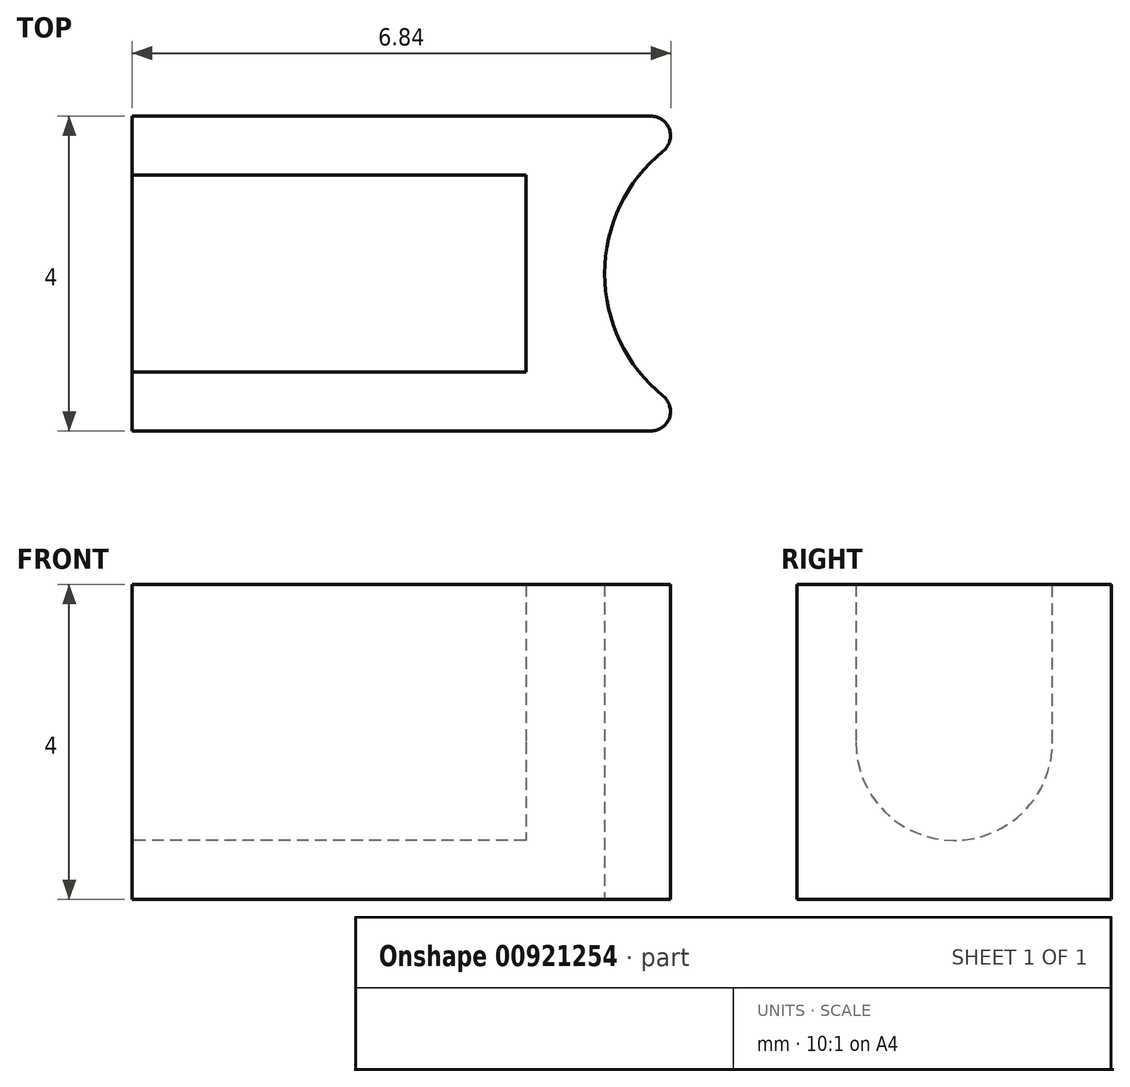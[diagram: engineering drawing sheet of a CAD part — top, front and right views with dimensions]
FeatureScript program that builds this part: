
annotation { "Feature Type Name" : "Feature", "Feature Type Description" : "" }
export const myFeature = defineFeature(function(context is Context, id is Id, definition is map)
    precondition{}
    {
        {
            var Q0;
            Q0=qCreatedBy(makeId("Top.planeOp"),FACE);
            var sketch = newSketch(context, id + "F0", { "sketchPlane" : qUnion([Q0])});
            skCircle(sketch, "E0", {"center": v(0, 0) * mm, "radius": 2 * mm});
            skLineSegment(sketch, "E1.bottom", {"start": v(0, 2) * mm, "end": v(-8, 2) * mm});
            skLineSegment(sketch, "E1.top", {"start": v(0, -2) * mm, "end": v(-8, -2) * mm});
            skLineSegment(sketch, "E1.left", {"start": v(0, 2) * mm, "end": v(0, -2) * mm});
            skLineSegment(sketch, "E1.right", {"start": v(-8, 2) * mm, "end": v(-8, -2) * mm});
            skSolve(sketch);
        }
        {
            var Q0;
            {var subQ1=sQuery(id+"F0.wireOp",EDGE,"E1.bottom");Q0=makeQuery(id+"F0.imprint","IMPRINT",FACE,{"disambiguationData":[TD([[makeQuery(id+"F0.imprint","IMPRINT",EDGE,{"derivedFrom":subQ1}),1.0]])]});}
            extrude(context, id + "F1", {"entities" : qUnion([Q0]), "depth" : 4 * mm, "offsetDistance" : 25 * mm});
        }
        {
            var Q0;
            Q0=makeQuery(id+"F1.opExtrude","SWEPT_FACE",FACE,{"disambiguationData":[OSD([sQuery(id+"F0.wireOp",EDGE,"E1.right")])]});
            var sketch = newSketch(context, id + "F2", { "sketchPlane" : qUnion([Q0])});
            skCircle(sketch, "E2", {"center": v(0, 2) * mm, "radius": 1.25 * mm});
            skPoint(sketch, "E2.centerSnap0", {"position": v(-2, 2) * mm});
            skLineSegment(sketch, "E3", {"start": v(-1.25, 2) * mm, "end": v(-1.25, 4) * mm});
            skLineSegment(sketch, "E4", {"start": v(-1.25, 4) * mm, "end": v(1.25, 4) * mm});
            skLineSegment(sketch, "E5", {"start": v(1.25, 4) * mm, "end": v(1.25, 2) * mm});
            skSolve(sketch);
        }
        {
            var Q0;
            Q0=makeQuery(id+"F2.imprint","IMPRINT",FACE,{"disambiguationData":[TD([[makeQuery(id+"F2.imprint","IMPRINT",EDGE,{"derivedFrom":sQuery(id+"F2.wireOp",EDGE,"E2")}),1.0]])]});
            var Q1;
            {var subQ0=sQuery(id+"F2.wireOp",EDGE,"E3");Q1=makeQuery(id+"F2.imprint","IMPRINT",FACE,{"disambiguationData":[TD([[makeQuery(id+"F2.imprint","IMPRINT",EDGE,{"derivedFrom":subQ0}),-1.0]])]});}
            extrude(context, id + "F3", {"entities" : qUnion([Q0, Q1]), "operationType" : NewBodyOperationType.REMOVE, "oppositeDirection" : true, "depth" : 5 * mm, "offsetDistance" : 25 * mm});
        }
        {
            var Q0;
            Q0=makeQuery(id+"F1.opExtrude","SWEPT_EDGE",EDGE,{"disambiguationData":[OSD([sQuery(id+"F0.wireOp",EDGE,"E0"),sQuery(id+"F0.wireOp",EDGE,"E1.bottom"),sQuery(id+"F0.wireOp",EDGE,"E1.left")])]});
            var Q1;
            Q1=makeQuery(id+"F1.opExtrude","SWEPT_EDGE",EDGE,{"disambiguationData":[OSD([sQuery(id+"F0.wireOp",EDGE,"E0"),sQuery(id+"F0.wireOp",EDGE,"E1.top"),sQuery(id+"F0.wireOp",EDGE,"E1.left")])]});
            fillet(context, id + "F4", {"entities" : qUnion([Q0, Q1]), "radius" : .25 * mm, "tangentPropagation" : true, "allowEdgeOverflow" : false});
        }
    });
